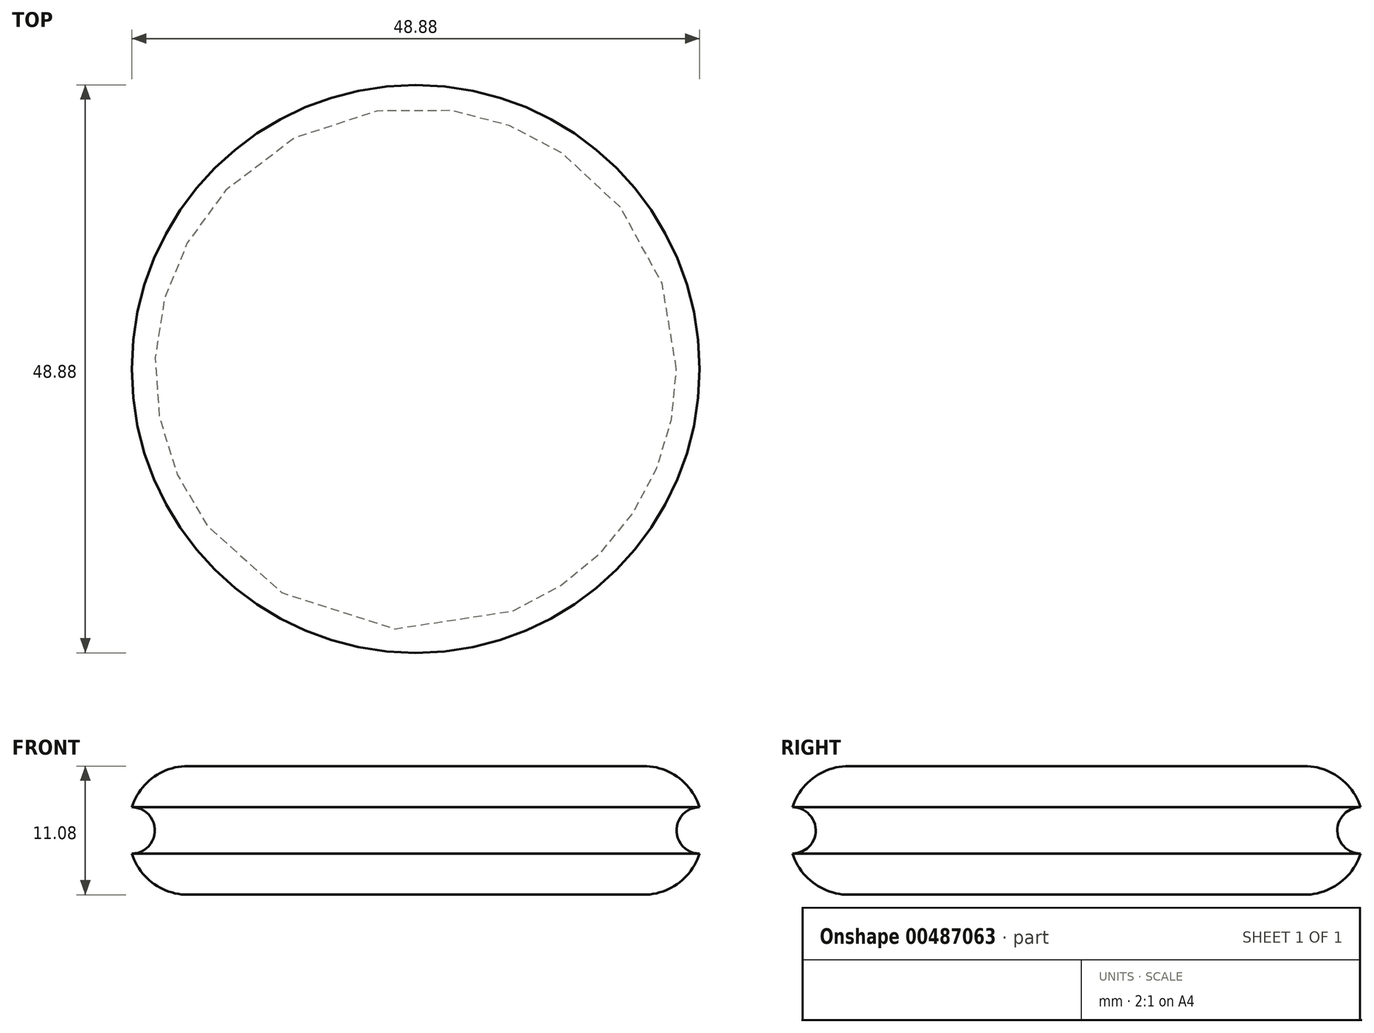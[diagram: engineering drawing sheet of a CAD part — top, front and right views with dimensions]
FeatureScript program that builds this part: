
annotation { "Feature Type Name" : "Feature", "Feature Type Description" : "" }
export const myFeature = defineFeature(function(context is Context, id is Id, definition is map)
    precondition{}
    {
        {
            var Q0;
            Q0=qCreatedBy(makeId("Front.planeOp"),FACE);
            var sketch = newSketch(context, id + "F0", { "sketchPlane" : qUnion([Q0])});
            skLineSegment(sketch, "E0.bottom", {"start": v(0, 0) * mm, "end": v(24.44, 0) * mm});
            skLineSegment(sketch, "E0.top", {"start": v(0, -11.08) * mm, "end": v(24.44, -11.08) * mm});
            skLineSegment(sketch, "E0.left", {"start": v(0, 0) * mm, "end": v(0, -11.08) * mm});
            skLineSegment(sketch, "E0.right", {"start": v(24.44, 0) * mm, "end": v(24.44, -3.54) * mm});
            skArc(sketch, "E1", {"start": v(24.44, -3.54) * mm, "mid": v(22.45, -5.54) * mm, "end": v(24.44, -7.53) * mm});
            skLineSegment(sketch, "E2.trimOffspring", {"start": v(24.44, -7.53) * mm, "end": v(24.44, -11.08) * mm});
            skSolve(sketch);
        }
        {
            var Q0;
            Q0=makeQuery(id+"F0.imprint","IMPRINT",FACE,{"disambiguationData":[TD([[makeQuery(id+"F0.imprint","IMPRINT",EDGE,{"derivedFrom":sQuery(id+"F0.wireOp",EDGE,"E0.bottom")}),-1.0]])]});
            var Q1;
            Q1=sQuery(id+"F0.wireOp",EDGE,"E0.left");
            revolve(context, id + "F1", {"entities" : qUnion([Q0]), "axis" : qUnion([Q1]), "revolveType" : RevolveType.FULL});
        }
        {
            var Q0;
            Q0=makeQuery(id+"F1.opRevolve","SWEPT_EDGE",EDGE,{"disambiguationData":[OSD([sQuery(id+"F0.wireOp",EDGE,"E0.bottom"),sQuery(id+"F0.wireOp",EDGE,"E0.right")])]});
            var Q1;
            Q1=makeQuery(id+"F1.opRevolve","SWEPT_EDGE",EDGE,{"disambiguationData":[OSD([sQuery(id+"F0.wireOp",EDGE,"E0.top"),sQuery(id+"F0.wireOp",EDGE,"E2.trimOffspring")])]});
            fillet(context, id + "F2", {"entities" : qUnion([Q0, Q1]), "radius" : 5.08 * mm, "tangentPropagation" : true, "allowEdgeOverflow" : false});
        }
    });
